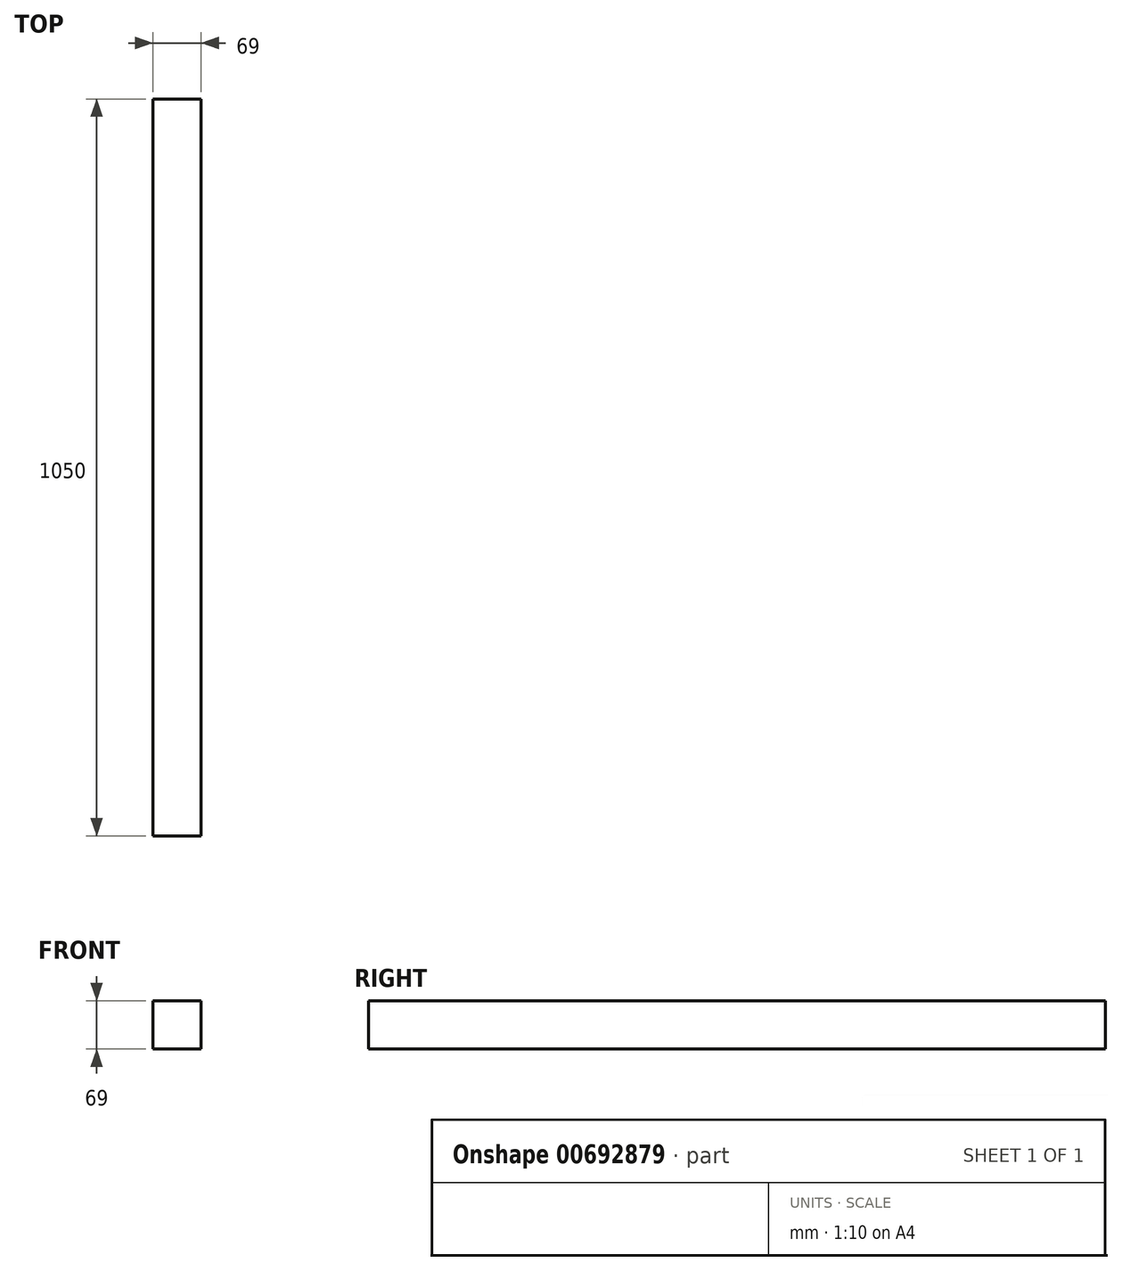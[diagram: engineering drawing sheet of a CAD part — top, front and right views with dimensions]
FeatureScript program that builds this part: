
annotation { "Feature Type Name" : "Feature", "Feature Type Description" : "" }
export const myFeature = defineFeature(function(context is Context, id is Id, definition is map)
    precondition{}
    {
        {
            var Q0;
            Q0=qCreatedBy(makeId("Front.planeOp"),FACE);
            var sketch = newSketch(context, id + "F0", { "sketchPlane" : qUnion([Q0])});
            skLineSegment(sketch, "E0.bottom", {"start": v(34.5, 34.5) * mm, "end": v(-34.5, 34.5) * mm});
            skLineSegment(sketch, "E0.top", {"start": v(34.5, -34.5) * mm, "end": v(-34.5, -34.5) * mm});
            skLineSegment(sketch, "E0.left", {"start": v(34.5, 34.5) * mm, "end": v(34.5, -34.5) * mm});
            skLineSegment(sketch, "E0.right", {"start": v(-34.5, 34.5) * mm, "end": v(-34.5, -34.5) * mm});
            skPoint(sketch, "E0.middle", {"position": v(0, 0) * mm});
            skSolve(sketch);
        }
        {
            var Q0;
            Q0 = qSketchRegion(id + "F0", true);
            extrude(context, id + "F1", {"entities" : qUnion([Q0]), "oppositeDirection" : true, "depth" : (1150 - 100) * mm, "offsetDistance" : 25 * mm});
        }
    });
